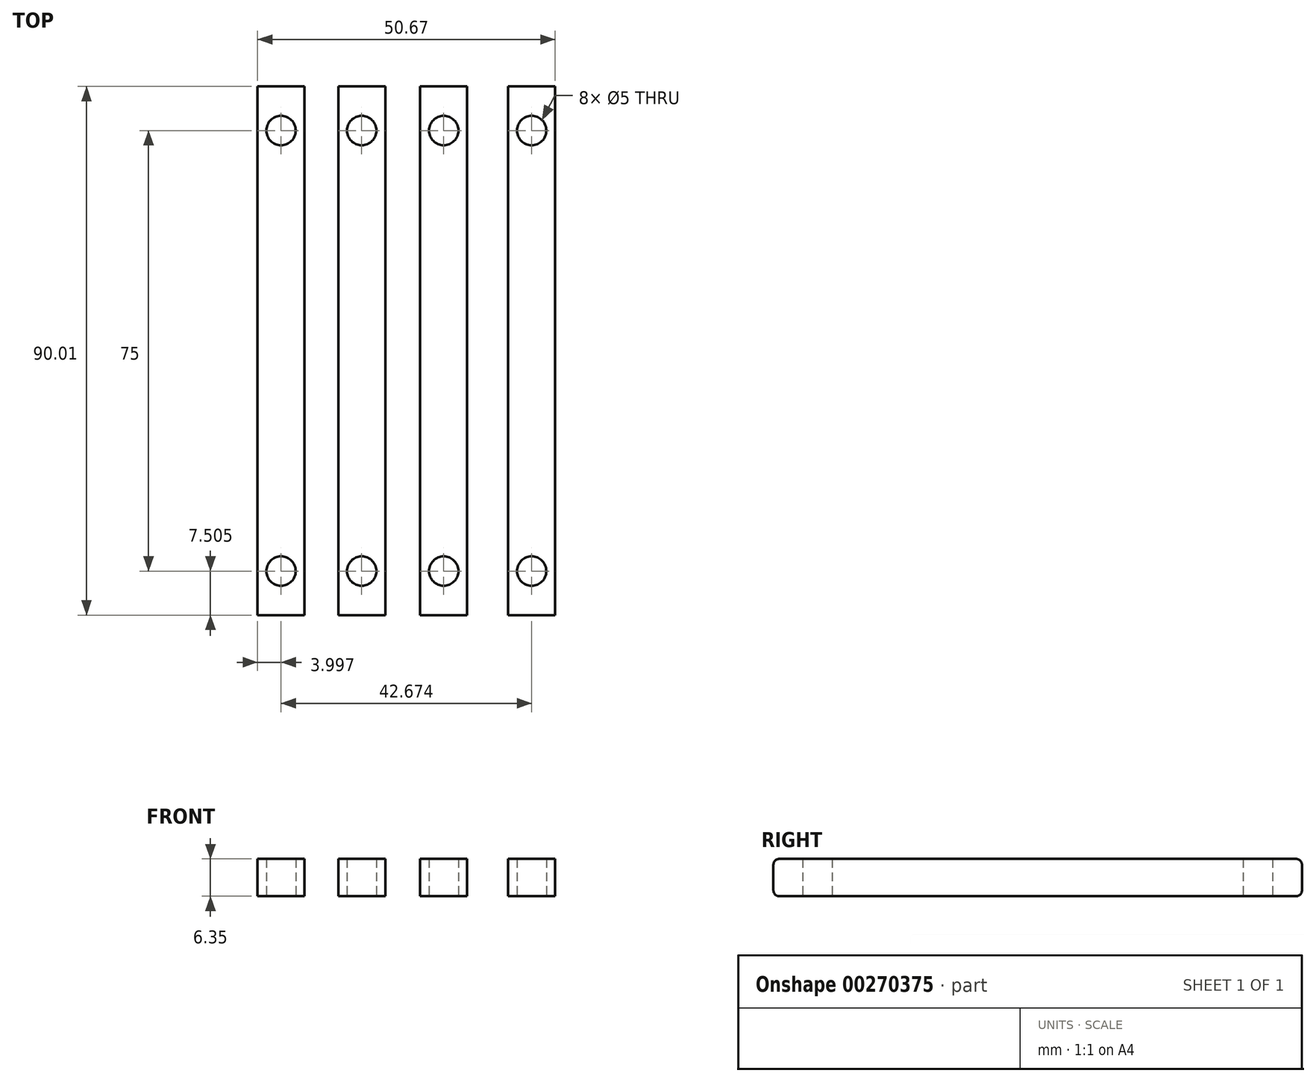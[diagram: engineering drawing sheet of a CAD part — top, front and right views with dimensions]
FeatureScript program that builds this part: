
annotation { "Feature Type Name" : "Feature", "Feature Type Description" : "" }
export const myFeature = defineFeature(function(context is Context, id is Id, definition is map)
    precondition{}
    {
        {
            var Q0;
            Q0=qCreatedBy(makeId("Top.planeOp"),FACE);
            var sketch = newSketch(context, id + "F0", { "sketchPlane" : qUnion([Q0])});
            skLineSegment(sketch, "E0.bottom", {"start": v(-23.5, 50.63) * mm, "end": v(-15.5, 50.63) * mm});
            skLineSegment(sketch, "E0.top", {"start": v(-23.5, -39.37) * mm, "end": v(-15.5, -39.37) * mm});
            skLineSegment(sketch, "E0.left", {"start": v(-23.5, 50.63) * mm, "end": v(-23.5, -39.37) * mm});
            skLineSegment(sketch, "E0.right", {"start": v(-15.5, 50.63) * mm, "end": v(-15.5, -39.37) * mm});
            skCircle(sketch, "E1", {"center": v(-19.5, 43.13) * mm, "radius": 2.5 * mm});
            skPoint(sketch, "E2.centerSnap0", {"position": v(-19.5, -39.37) * mm});
            skCircle(sketch, "E3.MirrorC", {"center": v(-19.5, -31.88) * mm, "radius": 2.5 * mm});
            skLineSegment(sketch, "E4.bottom", {"start": v(-9.77, 50.62) * mm, "end": v(-1.77, 50.62) * mm});
            skLineSegment(sketch, "E4.top", {"start": v(-9.77, -39.38) * mm, "end": v(-1.77, -39.38) * mm});
            skLineSegment(sketch, "E4.left", {"start": v(-9.77, 50.62) * mm, "end": v(-9.77, -39.38) * mm});
            skLineSegment(sketch, "E4.right", {"start": v(-1.77, 50.62) * mm, "end": v(-1.77, -39.38) * mm});
            skCircle(sketch, "E5", {"center": v(-5.76, 43.12) * mm, "radius": 2.5 * mm});
            skCircle(sketch, "E6.MirrorC", {"center": v(-5.76, -31.88) * mm, "radius": 2.5 * mm});
            skLineSegment(sketch, "E7.bottom", {"start": v(4.2, 50.62) * mm, "end": v(12.2, 50.62) * mm});
            skLineSegment(sketch, "E7.top", {"start": v(4.2, -39.38) * mm, "end": v(12.2, -39.38) * mm});
            skLineSegment(sketch, "E7.left", {"start": v(4.2, 50.62) * mm, "end": v(4.2, -39.38) * mm});
            skLineSegment(sketch, "E7.right", {"start": v(12.2, 50.62) * mm, "end": v(12.2, -39.38) * mm});
            skCircle(sketch, "E8", {"center": v(8.2, 43.12) * mm, "radius": 2.5 * mm});
            skLineSegment(sketch, "E9.bottom", {"start": v(19.17, 50.62) * mm, "end": v(27.17, 50.62) * mm});
            skLineSegment(sketch, "E9.top", {"start": v(19.17, -39.38) * mm, "end": v(27.17, -39.38) * mm});
            skLineSegment(sketch, "E9.left", {"start": v(19.17, 50.62) * mm, "end": v(19.17, -39.38) * mm});
            skLineSegment(sketch, "E9.right", {"start": v(27.17, 50.62) * mm, "end": v(27.17, -39.38) * mm});
            skCircle(sketch, "E10", {"center": v(23.17, 43.12) * mm, "radius": 2.5 * mm});
            skCircle(sketch, "E11.MirrorC", {"center": v(8.2, -31.88) * mm, "radius": 2.5 * mm});
            skCircle(sketch, "E12.MirrorC", {"center": v(23.17, -31.88) * mm, "radius": 2.5 * mm});
            skSolve(sketch);
        }
        {
            var Q0;
            Q0=makeQuery(id+"F0.imprint","IMPRINT",FACE,{"disambiguationData":[TD([[makeQuery(id+"F0.imprint","IMPRINT",EDGE,{"derivedFrom":sQuery(id+"F0.wireOp",EDGE,"E4.bottom")}),-1.0]])]});
            var Q1;
            Q1=makeQuery(id+"F0.imprint","IMPRINT",FACE,{"disambiguationData":[TD([[makeQuery(id+"F0.imprint","IMPRINT",EDGE,{"derivedFrom":sQuery(id+"F0.wireOp",EDGE,"E7.bottom")}),-1.0]])]});
            var Q2;
            Q2=makeQuery(id+"F0.imprint","IMPRINT",FACE,{"disambiguationData":[TD([[makeQuery(id+"F0.imprint","IMPRINT",EDGE,{"derivedFrom":sQuery(id+"F0.wireOp",EDGE,"E0.bottom")}),-1.0]])]});
            var Q3;
            Q3=makeQuery(id+"F0.imprint","IMPRINT",FACE,{"disambiguationData":[TD([[makeQuery(id+"F0.imprint","IMPRINT",EDGE,{"derivedFrom":sQuery(id+"F0.wireOp",EDGE,"E9.bottom")}),-1.0]])]});
            extrude(context, id + "F1", {"entities" : qUnion([Q0, Q1, Q2, Q3]), "depth" : 6.35 * mm});
        }
        {
            var Q0;
            Q0=makeQuery(id+"F1.opExtrude","CAP_EDGE",EDGE,{"disambiguationData":[OSD([sQuery(id+"F0.wireOp",EDGE,"E0.bottom")])],"isStart":false});
            var Q1;
            Q1=makeQuery(id+"F1.opExtrude","CAP_EDGE",EDGE,{"disambiguationData":[OSD([sQuery(id+"F0.wireOp",EDGE,"E4.bottom")])],"isStart":false});
            var Q2;
            Q2=makeQuery(id+"F1.opExtrude","CAP_EDGE",EDGE,{"disambiguationData":[OSD([sQuery(id+"F0.wireOp",EDGE,"E7.bottom")])],"isStart":false});
            var Q3;
            Q3=makeQuery(id+"F1.opExtrude","CAP_EDGE",EDGE,{"disambiguationData":[OSD([sQuery(id+"F0.wireOp",EDGE,"E9.bottom")])],"isStart":false});
            var Q4;
            Q4=makeQuery(id+"F1.opExtrude","CAP_EDGE",EDGE,{"disambiguationData":[OSD([sQuery(id+"F0.wireOp",EDGE,"E9.top")])],"isStart":false});
            var Q5;
            Q5=makeQuery(id+"F1.opExtrude","CAP_EDGE",EDGE,{"disambiguationData":[OSD([sQuery(id+"F0.wireOp",EDGE,"E7.top")])],"isStart":false});
            var Q6;
            Q6=makeQuery(id+"F1.opExtrude","CAP_EDGE",EDGE,{"disambiguationData":[OSD([sQuery(id+"F0.wireOp",EDGE,"E4.top")])],"isStart":false});
            var Q7;
            Q7=makeQuery(id+"F1.opExtrude","CAP_EDGE",EDGE,{"disambiguationData":[OSD([sQuery(id+"F0.wireOp",EDGE,"E0.top")])],"isStart":false});
            var Q8;
            Q8=makeQuery(id+"F1.opExtrude","CAP_EDGE",EDGE,{"disambiguationData":[OSD([sQuery(id+"F0.wireOp",EDGE,"E0.top")])],"isStart":true});
            var Q9;
            Q9=makeQuery(id+"F1.opExtrude","CAP_EDGE",EDGE,{"disambiguationData":[OSD([sQuery(id+"F0.wireOp",EDGE,"E4.top")])],"isStart":true});
            var Q10;
            Q10=makeQuery(id+"F1.opExtrude","CAP_EDGE",EDGE,{"disambiguationData":[OSD([sQuery(id+"F0.wireOp",EDGE,"E7.top")])],"isStart":true});
            var Q11;
            Q11=makeQuery(id+"F1.opExtrude","CAP_EDGE",EDGE,{"disambiguationData":[OSD([sQuery(id+"F0.wireOp",EDGE,"E9.top")])],"isStart":true});
            var Q12;
            Q12=makeQuery(id+"F1.opExtrude","CAP_EDGE",EDGE,{"disambiguationData":[OSD([sQuery(id+"F0.wireOp",EDGE,"E0.bottom")])],"isStart":true});
            var Q13;
            Q13=makeQuery(id+"F1.opExtrude","CAP_EDGE",EDGE,{"disambiguationData":[OSD([sQuery(id+"F0.wireOp",EDGE,"E4.bottom")])],"isStart":true});
            var Q14;
            Q14=makeQuery(id+"F1.opExtrude","CAP_EDGE",EDGE,{"disambiguationData":[OSD([sQuery(id+"F0.wireOp",EDGE,"E7.bottom")])],"isStart":true});
            var Q15;
            Q15=makeQuery(id+"F1.opExtrude","CAP_EDGE",EDGE,{"disambiguationData":[OSD([sQuery(id+"F0.wireOp",EDGE,"E9.bottom")])],"isStart":true});
            fillet(context, id + "F2", {"entities" : qUnion([Q0, Q1, Q2, Q3, Q4, Q5, Q6, Q7, Q8, Q9, Q10, Q11, Q12, Q13, Q14, Q15]), "radius" : 1 * mm, "tangentPropagation" : true, "allowEdgeOverflow" : false});
        }
    });
